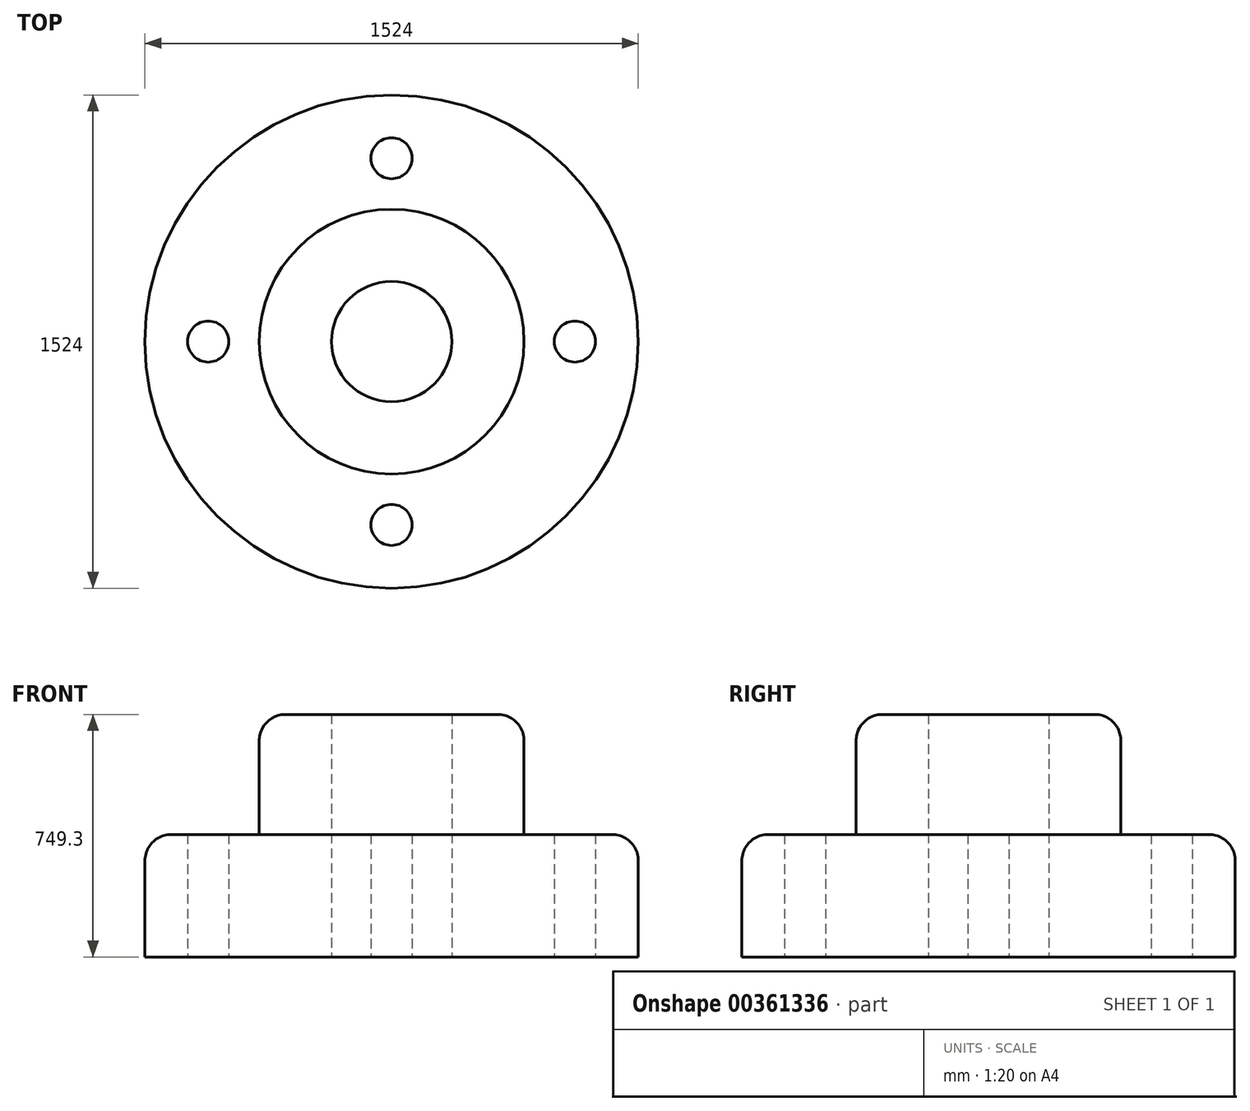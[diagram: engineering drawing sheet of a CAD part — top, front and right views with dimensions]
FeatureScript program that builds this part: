
annotation { "Feature Type Name" : "Feature", "Feature Type Description" : "" }
export const myFeature = defineFeature(function(context is Context, id is Id, definition is map)
    precondition{}
    {
        {
            var Q0;
            Q0=qCreatedBy(makeId("Top.planeOp"),FACE);
            var sketch = newSketch(context, id + "F0", { "sketchPlane" : qUnion([Q0])});
            skCircle(sketch, "E0", {"center": v(0, 0) * mm, "radius": 185.8 * mm});
            skCircle(sketch, "E1", {"center": v(0, 0) * mm, "radius": 408.94 * mm});
            skCircle(sketch, "E2", {"center": v(0, 0) * mm, "radius": 762 * mm});
            skCircle(sketch, "E3", {"center": v(-566.42, 0) * mm, "radius": 63.5 * mm});
            skCircle(sketch, "E4", {"center": v(566.42, 0) * mm, "radius": 63.5 * mm});
            skCircle(sketch, "E5", {"center": v(0, 566.42) * mm, "radius": 63.5 * mm});
            skCircle(sketch, "E6", {"center": v(0, -566.42) * mm, "radius": 63.5 * mm});
            skSolve(sketch);
        }
        {
            var Q0;
            Q0=makeQuery(id+"F0.imprint","IMPRINT",FACE,{"disambiguationData":[TD([[makeQuery(id+"F0.imprint","IMPRINT",EDGE,{"derivedFrom":sQuery(id+"F0.wireOp",EDGE,"E0")}),-1.0]])]});
            extrude(context, id + "F1", {"entities" : qUnion([Q0]), "depth" : 749.3 * mm});
        }
        {
            var Q0;
            Q0=makeQuery(id+"F0.imprint","IMPRINT",FACE,{"disambiguationData":[TD([[makeQuery(id+"F0.imprint","IMPRINT",EDGE,{"derivedFrom":sQuery(id+"F0.wireOp",EDGE,"E1")}),-1.0]])]});
            extrude(context, id + "F2", {"entities" : qUnion([Q0]), "operationType" : NewBodyOperationType.ADD, "depth" : 378.46 * mm});
        }
        {
            var Q0;
            Q0=makeQuery(id+"F1.opExtrude","CAP_EDGE",EDGE,{"disambiguationData":[OSD([sQuery(id+"F0.wireOp",EDGE,"E1")])],"isStart":false});
            fillet(context, id + "F3", {"entities" : qUnion([Q0]), "radius" : 81.28 * mm, "tangentPropagation" : true, "allowEdgeOverflow" : false});
        }
        {
            var Q0;
            Q0=makeQuery(id+"F2.opExtrude","CAP_EDGE",EDGE,{"disambiguationData":[OSD([sQuery(id+"F0.wireOp",EDGE,"E2")])],"isStart":false});
            fillet(context, id + "F4", {"entities" : qUnion([Q0]), "radius" : 81.28 * mm, "tangentPropagation" : true, "allowEdgeOverflow" : false});
        }
    });
